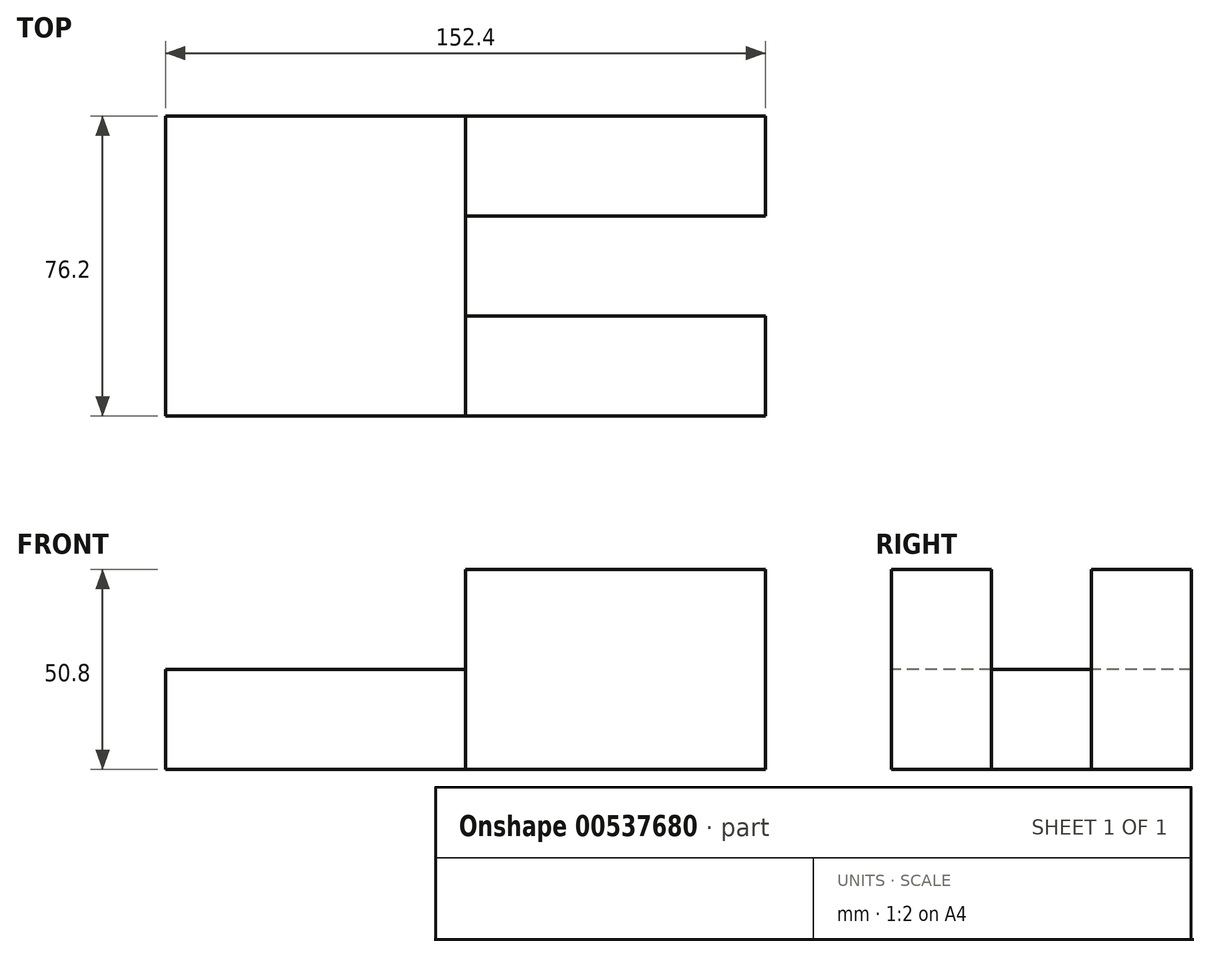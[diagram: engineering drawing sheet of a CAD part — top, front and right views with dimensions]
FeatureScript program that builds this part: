
annotation { "Feature Type Name" : "Feature", "Feature Type Description" : "" }
export const myFeature = defineFeature(function(context is Context, id is Id, definition is map)
    precondition{}
    {
        {
            var Q0;
            Q0=qCreatedBy(makeId("Top.planeOp"),FACE);
            var sketch = newSketch(context, id + "F0", { "sketchPlane" : qUnion([Q0])});
            skLineSegment(sketch, "E0.bottom", {"start": v(-79.73, 18.02) * mm, "end": v(-3.53, 18.02) * mm});
            skLineSegment(sketch, "E0.top", {"start": v(-79.73, -58.18) * mm, "end": v(-3.53, -58.18) * mm});
            skLineSegment(sketch, "E0.left", {"start": v(-79.73, 18.02) * mm, "end": v(-79.73, -58.18) * mm});
            skLineSegment(sketch, "E0.right", {"start": v(-3.53, 18.02) * mm, "end": v(-3.53, -58.18) * mm});
            skLineSegment(sketch, "E1.bottom", {"start": v(-3.53, 18.02) * mm, "end": v(72.67, 18.02) * mm});
            skLineSegment(sketch, "E1.top", {"start": v(-3.53, -7.38) * mm, "end": v(72.67, -7.38) * mm});
            skLineSegment(sketch, "E1.left", {"start": v(-3.53, 18.02) * mm, "end": v(-3.53, -7.38) * mm});
            skLineSegment(sketch, "E1.right", {"start": v(72.67, 18.02) * mm, "end": v(72.67, -7.38) * mm});
            skLineSegment(sketch, "E2.top", {"start": v(-3.53, -32.78) * mm, "end": v(72.67, -32.78) * mm});
            skLineSegment(sketch, "E2.left", {"start": v(-3.53, -7.38) * mm, "end": v(-3.53, -32.78) * mm});
            skLineSegment(sketch, "E2.right", {"start": v(72.67, -7.38) * mm, "end": v(72.67, -32.78) * mm});
            skLineSegment(sketch, "E3.top", {"start": v(-3.53, -58.18) * mm, "end": v(72.67, -58.18) * mm});
            skLineSegment(sketch, "E3.left", {"start": v(-3.53, -32.78) * mm, "end": v(-3.53, -58.18) * mm});
            skLineSegment(sketch, "E3.right", {"start": v(72.67, -32.78) * mm, "end": v(72.67, -58.18) * mm});
            skSolve(sketch);
        }
        {
            var Q0;
            Q0=makeQuery(id+"F0.imprint","IMPRINT",FACE,{"disambiguationData":[TD([[makeQuery(id+"F0.imprint","IMPRINT",EDGE,{"derivedFrom":sQuery(id+"F0.wireOp",EDGE,"E1.bottom")}),-1.0]])]});
            var Q1;
            Q1=makeQuery(id+"F0.imprint","IMPRINT",FACE,{"disambiguationData":[TD([[makeQuery(id+"F0.imprint","IMPRINT",EDGE,{"derivedFrom":sQuery(id+"F0.wireOp",EDGE,"E2.top")}),-1.0]])]});
            extrude(context, id + "F1", {"entities" : qUnion([Q0, Q1]), "depth" : 50.8 * mm, "offsetDistance" : 25.4 * mm});
        }
        {
            var Q0;
            Q0=makeQuery(id+"F0.imprint","IMPRINT",FACE,{"disambiguationData":[TD([[makeQuery(id+"F0.imprint","IMPRINT",EDGE,{"derivedFrom":sQuery(id+"F0.wireOp",EDGE,"E0.bottom")}),-1.0]])]});
            var Q1;
            Q1=makeQuery(id+"F0.imprint","IMPRINT",FACE,{"disambiguationData":[TD([[makeQuery(id+"F0.imprint","IMPRINT",EDGE,{"derivedFrom":sQuery(id+"F0.wireOp",EDGE,"E1.top")}),-1.0]])]});
            extrude(context, id + "F2", {"entities" : qUnion([Q0, Q1]), "depth" : 25.4 * mm, "offsetDistance" : 25.4 * mm});
        }
    });
